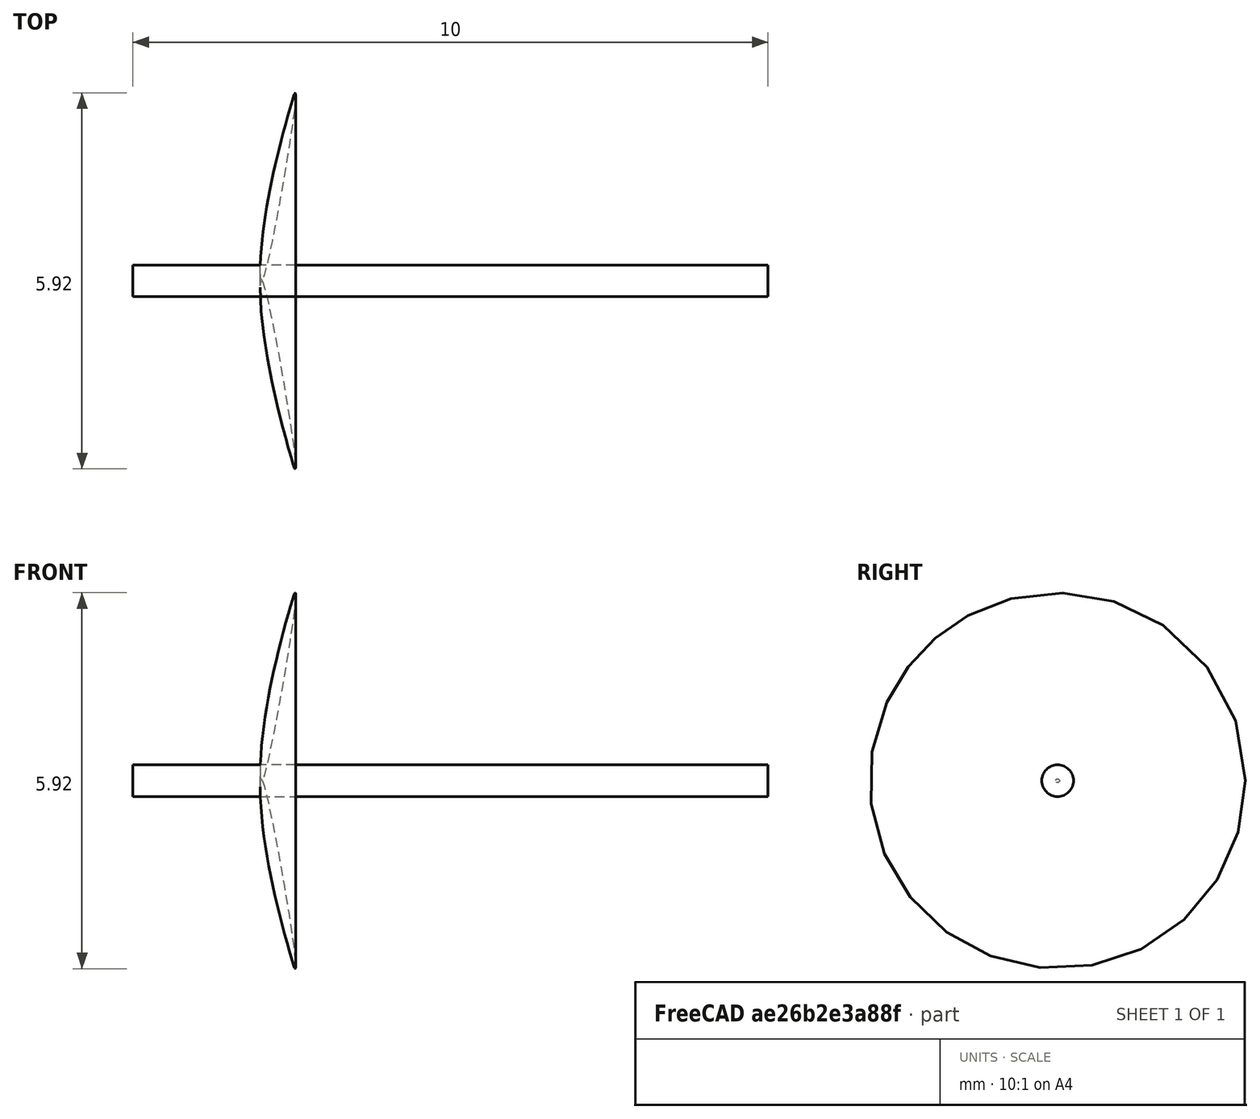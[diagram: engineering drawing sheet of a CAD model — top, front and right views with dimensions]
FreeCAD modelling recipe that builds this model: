
FCSTD DOCUMENT  (FreeCAD 0.21R0.21.2)
Label: PierceAnode
License: All rights reserved
LicenseURL: http://en.wikipedia.org/wiki/All_rights_reserved
objects: Part::FeaturePython×1, PartDesign::Revolution×1, PartDesign::Body×1, Part::Cylinder×1
note: 5 computed .brp shape members not serialized (recipe doc carries the construction recipe); baked Part::Feature solids carry a one-line shape summary decoded from their .brp

FEATURE [Part::FeaturePython] ParametricCurve  # WARN: FeaturePython — macro-defined, semantics opaque (R4)
  AttacherType = Attacher::AttachEngine3D
  Closed = true
  Continuity = C2
  EditFormulas = false
  F_X = 0
  F_Y = 0
  F_Z = 0
  F_a = 1
  F_b = 5
  F_c = 1
  F_d = [0,20,1,0,0,0]
  FormulaName = helix
  Formulas = 0
  Interval = 0.01
  MakeFace = false
  PlusOneIteration = true
  Points = (81) [(2.00083,0.100125,0),(2.0012,0.120216,0),(2.00164,0.140344,0),(2.00214,0.160514,0),(2.00272,0.180733,0),(2.00336,0.201006,0),(2.00407,0.221341,0),+74 more]
  ShapeType = 0
  Sorted = false
  UpdateSpreadsheet = false
  UseSpreadsheet = false
  Version = 2024.05.08b
  X = 2 * ( cos(4/3 * t) ^ (-3/4)) * cos(t)
  Y = 2 * ( cos(4/3 * t) ^ (-3/4)) * sin(t)
  Z = 0
  a = 1  #pitch
  b = 5 #height
  c = 1 #base radius
  d = {d1} 20 #angle deg | {d2} 1  # 1= RH  0 = LH | {d3} t*b/a | {d4} c + b*t*sin(rad(d1))/(2*pi) | {d5} ternary(d2, 1, -1)
  t_max = 0.85
  t_min = 0.05
FEATURE [PartDesign::Revolution] Revolution
  Angle = 360
  Axis = (1,0,0)
  Base = (0,0,0)
  Profile = -> ParametricCurve
  ReferenceAxis = -> X_Axis
  Reversed = true
FEATURE [PartDesign::Body] Body
  Group = -> [ParametricCurve,Revolution]
  Origin = -> Origin
  Tip = -> Revolution
FEATURE [Part::Cylinder] Cylinder001  label="Beamhole"
  Angle = 360
  AttacherType = Attacher::AttachEngine3D
  FirstAngle = 0
  Height = 10
  Placement = pos=(0,0,0) rot=(0,1,0;1.5708rad)
  Radius = 0.25
  SecondAngle = 0
